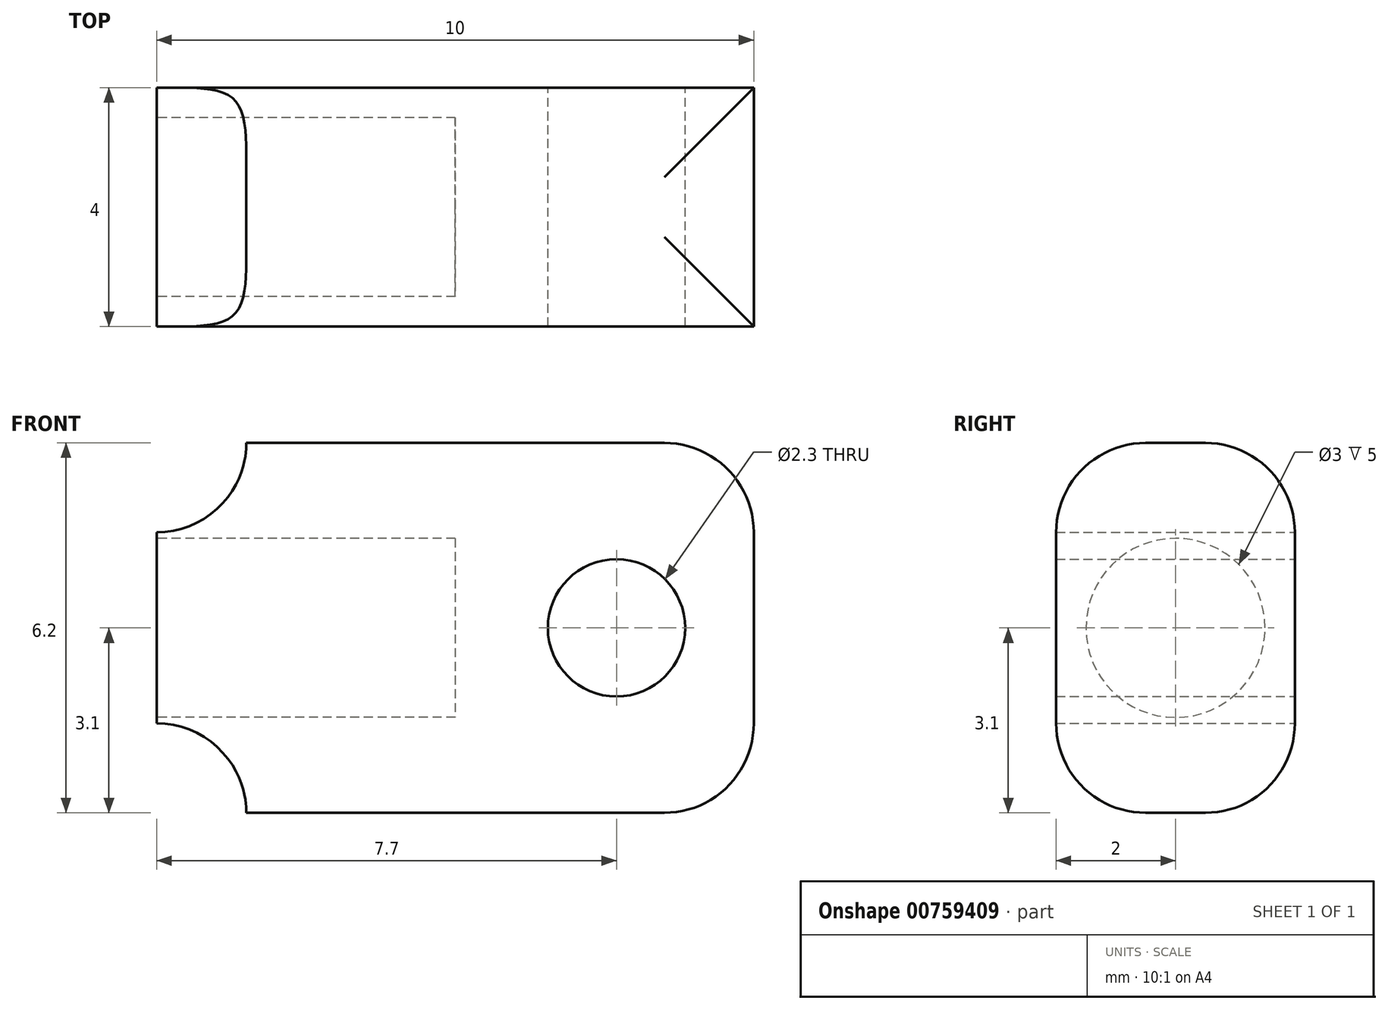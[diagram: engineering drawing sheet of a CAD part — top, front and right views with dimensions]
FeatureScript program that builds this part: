
annotation { "Feature Type Name" : "Feature", "Feature Type Description" : "" }
export const myFeature = defineFeature(function(context is Context, id is Id, definition is map)
    precondition{}
    {
        {
            var Q0;
            Q0=qCreatedBy(makeId("Front.planeOp"),FACE);
            var sketch = newSketch(context, id + "F0", { "sketchPlane" : qUnion([Q0])});
            skPoint(sketch, "E0.middle", {"position": v(0, 0) * mm});
            skLineSegment(sketch, "E1.bottom", {"start": v(-3.5, 3.1) * mm, "end": v(5, 3.1) * mm});
            skLineSegment(sketch, "E1.top", {"start": v(-3.5, -3.1) * mm, "end": v(5, -3.1) * mm});
            skLineSegment(sketch, "E1.left", {"start": v(-5, 1.6) * mm, "end": v(-5, -1.6) * mm});
            skLineSegment(sketch, "E1.right", {"start": v(5, 3.1) * mm, "end": v(5, -3.1) * mm});
            skArc(sketch, "E2", {"start": v(-5, 1.6) * mm, "mid": v(-3.94, 2.04) * mm, "end": v(-3.5, 3.1) * mm});
            skArc(sketch, "E3.MirrorCS", {"start": v(-5, -1.6) * mm, "mid": v(-3.94, -2.04) * mm, "end": v(-3.5, -3.1) * mm});
            skCircle(sketch, "E4", {"center": v(2.7, 0) * mm, "radius": 1.15 * mm});
            skSolve(sketch);
        }
        {
            var Q0;
            Q0 = qSketchRegion(id + "F0", true);
            extrude(context, id + "F1", {"entities" : qUnion([Q0]), "depth" : 4 * mm, "offsetDistance" : 25 * mm});
        }
        {
            var Q0;
            Q0=makeQuery(id+"F1.opExtrude","SWEPT_FACE",FACE,{"disambiguationData":[OSD([sQuery(id+"F0.wireOp",EDGE,"E1.left")])]});
            var sketch = newSketch(context, id + "F2", { "sketchPlane" : qUnion([Q0])});
            skCircle(sketch, "E5", {"center": v(2, 0) * mm, "radius": 1.5 * mm});
            skPoint(sketch, "E5.centerSnap0", {"position": v(2, 1.6) * mm});
            skSolve(sketch);
        }
        {
            var Q0;
            Q0 = qSketchRegion(id + "F2", true);
            extrude(context, id + "F3", {"entities" : qUnion([Q0]), "operationType" : NewBodyOperationType.REMOVE, "oppositeDirection" : true, "depth" : 5 * mm, "offsetDistance" : 25 * mm});
        }
        {
            var Q0;
            Q0=makeQuery(id+"F1.opExtrude","SWEPT_EDGE",EDGE,{"disambiguationData":[OSD([sQuery(id+"F0.wireOp",EDGE,"E1.bottom"),sQuery(id+"F0.wireOp",EDGE,"E1.right")])]});
            var Q1;
            Q1=makeQuery(id+"F1.opExtrude","CAP_EDGE",EDGE,{"disambiguationData":[OSD([sQuery(id+"F0.wireOp",EDGE,"E1.bottom")])],"isStart":false});
            var Q2;
            Q2=makeQuery(id+"F1.opExtrude","CAP_EDGE",EDGE,{"disambiguationData":[OSD([sQuery(id+"F0.wireOp",EDGE,"E1.bottom")])],"isStart":true});
            var Q3;
            Q3=makeQuery(id+"F1.opExtrude","CAP_EDGE",EDGE,{"disambiguationData":[OSD([sQuery(id+"F0.wireOp",EDGE,"E1.top")])],"isStart":false});
            var Q4;
            Q4=makeQuery(id+"F1.opExtrude","SWEPT_EDGE",EDGE,{"disambiguationData":[OSD([sQuery(id+"F0.wireOp",EDGE,"E1.top"),sQuery(id+"F0.wireOp",EDGE,"E1.right")])]});
            var Q5;
            Q5=makeQuery(id+"F1.opExtrude","CAP_EDGE",EDGE,{"disambiguationData":[OSD([sQuery(id+"F0.wireOp",EDGE,"E1.top")])],"isStart":true});
            fillet(context, id + "F4", {"entities" : qUnion([Q0, Q1, Q2, Q3, Q4, Q5]), "radius" : 1.5 * mm, "tangentPropagation" : true, "allowEdgeOverflow" : false});
        }
    });
